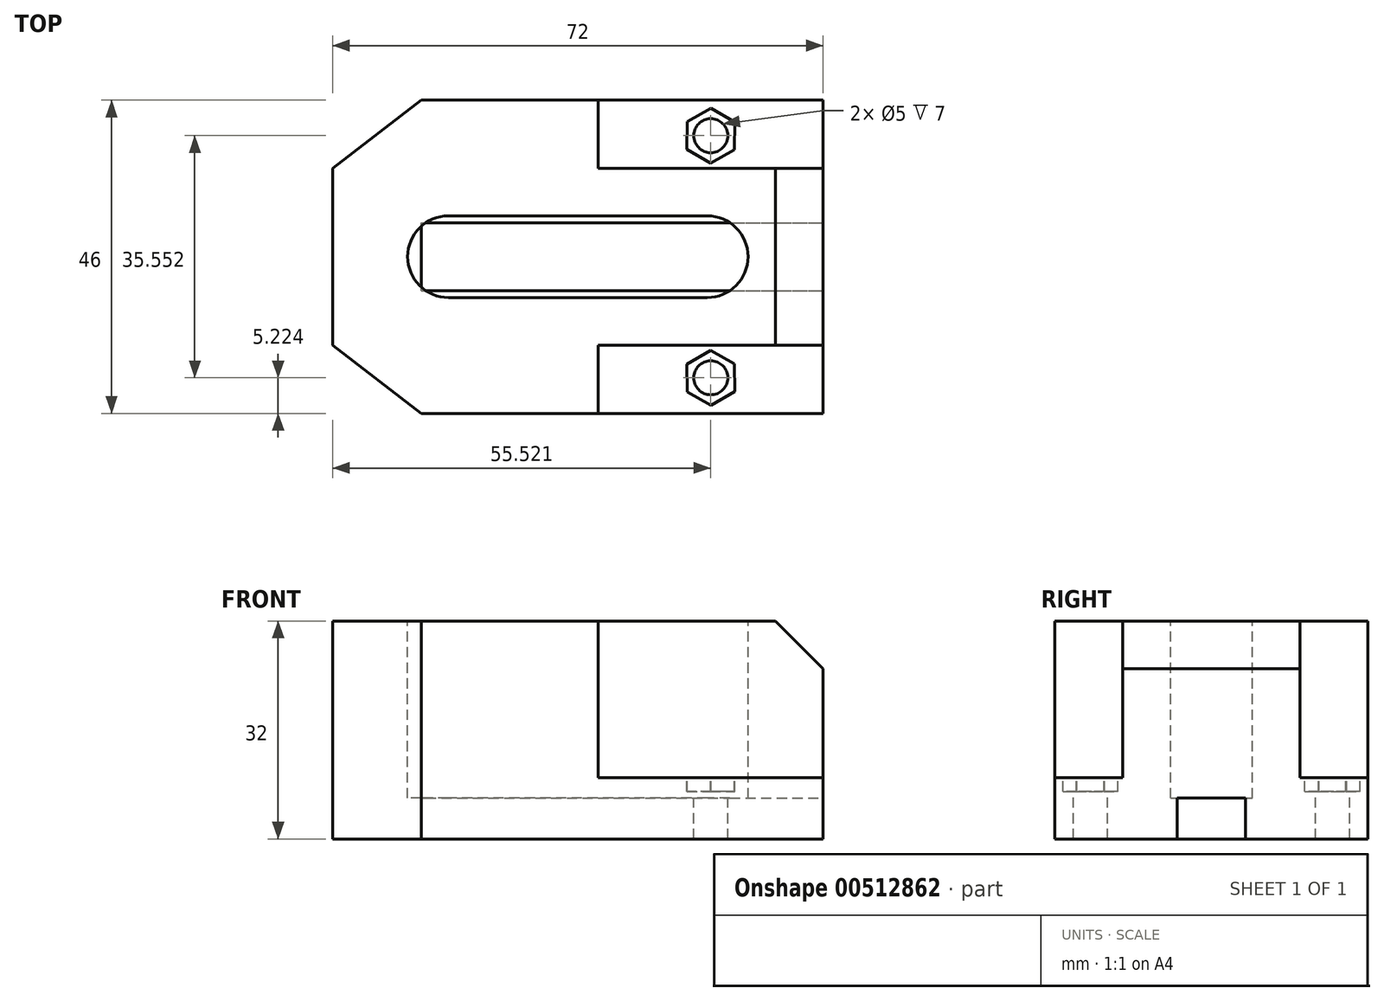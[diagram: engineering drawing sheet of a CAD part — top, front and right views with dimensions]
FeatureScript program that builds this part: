
annotation { "Feature Type Name" : "Feature", "Feature Type Description" : "" }
export const myFeature = defineFeature(function(context is Context, id is Id, definition is map)
    precondition{}
    {
        {
            var Q0;
            Q0=qCreatedBy(makeId("Top.planeOp"),FACE);
            var sketch = newSketch(context, id + "F0", { "sketchPlane" : qUnion([Q0])});
            skLineSegment(sketch, "E0.bottom", {"start": v(29.5, -23) * mm, "end": v(-29.5, -23) * mm});
            skLineSegment(sketch, "E0.top", {"start": v(29.5, 23) * mm, "end": v(-29.5, 23) * mm});
            skLineSegment(sketch, "E0.left", {"start": v(29.5, -23) * mm, "end": v(29.5, 23) * mm});
            skLineSegment(sketch, "E0.right", {"start": v(-29.5, -23) * mm, "end": v(-29.5, 23) * mm});
            skPoint(sketch, "E0.middle", {"position": v(0, 0) * mm});
            skSolve(sketch);
        }
        {
            var Q0;
            Q0 = qSketchRegion(id + "F0", true);
            extrude(context, id + "F1", {"entities" : qUnion([Q0]), "depth" : 32 * mm});
        }
        {
            var Q0;
            Q0=makeQuery(id+"F1.opExtrude","SWEPT_FACE",FACE,{"disambiguationData":[OSD([sQuery(id+"F0.wireOp",EDGE,"E0.left")])]});
            var sketch = newSketch(context, id + "F2", { "sketchPlane" : qUnion([Q0])});
            skLineSegment(sketch, "E1.bottom", {"start": v(-5, 0) * mm, "end": v(5, 0) * mm});
            skLineSegment(sketch, "E1.top", {"start": v(-5, 6) * mm, "end": v(5, 6) * mm});
            skLineSegment(sketch, "E1.left", {"start": v(-5, 0) * mm, "end": v(-5, 6) * mm});
            skLineSegment(sketch, "E1.right", {"start": v(5, 0) * mm, "end": v(5, 6) * mm});
            skSolve(sketch);
        }
        {
            var Q0;
            Q0 = qSketchRegion(id + "F2", true);
            extrude(context, id + "F3", {"entities" : qUnion([Q0]), "operationType" : NewBodyOperationType.REMOVE, "oppositeDirection" : true, "depth" : 59 * mm});
        }
        {
            var Q0;
            Q0=makeQuery(id+"F1.opExtrude","CAP_FACE",FACE,{"disambiguationData":[OSD([sQuery(id+"F0.wireOp",EDGE,"E0.bottom"),sQuery(id+"F0.wireOp",EDGE,"E0.top"),sQuery(id+"F0.wireOp",EDGE,"E0.left"),sQuery(id+"F0.wireOp",EDGE,"E0.right")])],"isStart":false});
            var sketch = newSketch(context, id + "F4", { "sketchPlane" : qUnion([Q0])});
            skLineSegment(sketch, "E2.bottom", {"start": v(29.5, -23) * mm, "end": v(-3.5, -23) * mm});
            skLineSegment(sketch, "E2.top", {"start": v(29.5, -13) * mm, "end": v(-3.5, -13) * mm});
            skLineSegment(sketch, "E2.left", {"start": v(29.5, -23) * mm, "end": v(29.5, -13) * mm});
            skLineSegment(sketch, "E2.right", {"start": v(-3.5, -23) * mm, "end": v(-3.5, -13) * mm});
            skLineSegment(sketch, "E3", {"start": v(0, 0) * mm, "end": v(-20.52, 0) * mm, "construction": true});
            skLineSegment(sketch, "E4.MirrorCS", {"start": v(29.5, 13) * mm, "end": v(-3.5, 13) * mm});
            skLineSegment(sketch, "E5.MirrorCS", {"start": v(-3.5, 23) * mm, "end": v(-3.5, 13) * mm});
            skLineSegment(sketch, "E6.MirrorCS", {"start": v(29.5, 23) * mm, "end": v(-3.5, 23) * mm});
            skLineSegment(sketch, "E7.MirrorCS", {"start": v(29.5, 23) * mm, "end": v(29.5, 13) * mm});
            skLineSegment(sketch, "E8", {"start": v(-42.5, -13) * mm, "end": v(-42.5, 13) * mm});
            skLineSegment(sketch, "E9", {"start": v(-42.5, -13) * mm, "end": v(-29.5, -23) * mm});
            skLineSegment(sketch, "E10", {"start": v(-42.5, 13) * mm, "end": v(-29.5, 23) * mm});
            skSolve(sketch);
        }
        {
            var Q0;
            Q0 = qSketchRegion(id + "F4", true);
            extrude(context, id + "F5", {"entities" : qUnion([Q0]), "operationType" : NewBodyOperationType.REMOVE, "oppositeDirection" : true, "depth" : 23 * mm});
        }
        {
            var Q0;
            Q0=makeQuery(id+"F4.imprint","IMPRINT",FACE,{"disambiguationData":[TD([[makeQuery(id+"F4.imprint","IMPRINT",EDGE,{"derivedFrom":sQuery(id+"F4.wireOp",EDGE,"E8")}),-1.0]])]});
            extrude(context, id + "F6", {"entities" : qUnion([Q0]), "operationType" : NewBodyOperationType.ADD, "oppositeDirection" : true, "depth" : 32 * mm});
        }
        {
            var Q0;
            Q0=makeQuery(id+"F5.boolean.opBoolean","COPY",FACE,{"derivedFrom":makeQuery(id+"F5.opExtrude","SWEPT_FACE",FACE,{"disambiguationData":[OSD([sQuery(id+"F4.wireOp",EDGE,"E2.top")])]})});
            var sketch = newSketch(context, id + "F7", { "sketchPlane" : qUnion([Q0])});
            skLineSegment(sketch, "E11", {"start": v(29.5, 32) * mm, "end": v(29.5, 25) * mm});
            skLineSegment(sketch, "E12", {"start": v(29.5, 25) * mm, "end": v(22.5, 32) * mm});
            skLineSegment(sketch, "E13", {"start": v(22.5, 32) * mm, "end": v(29.5, 32) * mm});
            skSolve(sketch);
        }
        {
            var Q0;
            Q0 = qSketchRegion(id + "F7", true);
            extrude(context, id + "F8", {"entities" : qUnion([Q0]), "operationType" : NewBodyOperationType.REMOVE, "oppositeDirection" : true, "depth" : 26 * mm});
        }
        {
            var Q0;
            {var subQ4=sQuery(id+"F4.wireOp",EDGE,"E2.top");Q0=makeQuery(id+"F4.imprint","IMPRINT",FACE,{"disambiguationData":[TD([[makeQuery(id+"F4.imprint","IMPRINT",EDGE,{"derivedFrom":subQ4}),-1.0]])]});}
            var sketch = newSketch(context, id + "F9", { "sketchPlane" : qUnion([Q0])});
            skLineSegment(sketch, "E14", {"start": v(-3.5, 13) * mm, "end": v(-3.5, -13) * mm});
            skLineSegment(sketch, "E15.bottom", {"start": v(12.5, -6) * mm, "end": v(-25.5, -6) * mm});
            skLineSegment(sketch, "E15.top", {"start": v(12.5, 6) * mm, "end": v(-25.5, 6) * mm});
            skLineSegment(sketch, "E15.left", {"start": v(12.5, -6) * mm, "end": v(12.5, 6) * mm});
            skLineSegment(sketch, "E15.right", {"start": v(-25.5, -6) * mm, "end": v(-25.5, 6) * mm});
            skArc(sketch, "E16", {"start": v(12.5, -6) * mm, "mid": v(18.5, 0) * mm, "end": v(12.5, 6) * mm});
            skArc(sketch, "E17", {"start": v(-25.5, 6) * mm, "mid": v(-31.5, 0) * mm, "end": v(-25.5, -6) * mm});
            skSolve(sketch);
        }
        {
            var Q0;
            Q0 = qSketchRegion(id + "F9", true);
            extrude(context, id + "F10", {"entities" : qUnion([Q0]), "operationType" : NewBodyOperationType.REMOVE, "oppositeDirection" : true, "depth" : 26 * mm});
        }
        {
            var Q0;
            Q0=makeQuery(id+"F5.boolean.opBoolean","COPY",FACE,{"derivedFrom":makeQuery(id+"F5.opExtrude","CAP_FACE",FACE,{"disambiguationData":[OSD([sQuery(id+"F4.wireOp",EDGE,"E2.bottom"),sQuery(id+"F4.wireOp",EDGE,"E2.top"),sQuery(id+"F4.wireOp",EDGE,"E2.left"),sQuery(id+"F4.wireOp",EDGE,"E2.right")])],"isStart":false})});
            var sketch = newSketch(context, id + "F11", { "sketchPlane" : qUnion([Q0])});
            skCircle(sketch, "E18.cCircle", {"center": v(13.02, -17.78) * mm, "radius": 3.5 * mm, "construction": true});
            skLineSegment(sketch, "E18.0", {"start": v(12.98, -13.73) * mm, "end": v(16.5, -15.72) * mm});
            skLineSegment(sketch, "E18.1", {"start": v(16.5, -15.72) * mm, "end": v(16.54, -19.76) * mm});
            skLineSegment(sketch, "E18.2", {"start": v(16.54, -19.76) * mm, "end": v(13.06, -21.82) * mm});
            skLineSegment(sketch, "E18.3", {"start": v(13.06, -21.82) * mm, "end": v(9.54, -19.83) * mm});
            skLineSegment(sketch, "E18.4", {"start": v(9.54, -19.83) * mm, "end": v(9.5, -15.8) * mm});
            skLineSegment(sketch, "E18.5", {"start": v(9.5, -15.8) * mm, "end": v(12.98, -13.73) * mm});
            skPoint(sketch, "E18.0.midPoint", {"position": v(14.74, -14.73) * mm});
            skCircle(sketch, "E19.MirrorC", {"center": v(13.02, 17.78) * mm, "radius": 3.5 * mm, "construction": true});
            skLineSegment(sketch, "E20.MirrorCS", {"start": v(9.54, 19.83) * mm, "end": v(9.5, 15.8) * mm});
            skLineSegment(sketch, "E21.MirrorCS", {"start": v(9.5, 15.8) * mm, "end": v(12.98, 13.73) * mm});
            skLineSegment(sketch, "E22.MirrorCS", {"start": v(12.98, 13.73) * mm, "end": v(16.5, 15.72) * mm});
            skLineSegment(sketch, "E23.MirrorCS", {"start": v(16.5, 15.72) * mm, "end": v(16.54, 19.76) * mm});
            skLineSegment(sketch, "E24.MirrorCS", {"start": v(16.54, 19.76) * mm, "end": v(13.06, 21.82) * mm});
            skLineSegment(sketch, "E25.MirrorCS", {"start": v(13.06, 21.82) * mm, "end": v(9.54, 19.83) * mm});
            skSolve(sketch);
        }
        {
            var Q0;
            Q0 = qSketchRegion(id + "F11", true);
            extrude(context, id + "F12", {"entities" : qUnion([Q0]), "operationType" : NewBodyOperationType.REMOVE, "oppositeDirection" : true, "depth" : 2 * mm});
        }
        {
            var Q0;
            Q0=makeQuery(id+"F12.boolean.opBoolean","COPY",FACE,{"derivedFrom":makeQuery(id+"F12.opExtrude","CAP_FACE",FACE,{"disambiguationData":[OSD([sQuery(id+"F11.wireOp",EDGE,"E18.0"),sQuery(id+"F11.wireOp",EDGE,"E18.1"),sQuery(id+"F11.wireOp",EDGE,"E18.2"),sQuery(id+"F11.wireOp",EDGE,"E18.3"),sQuery(id+"F11.wireOp",EDGE,"E18.4"),sQuery(id+"F11.wireOp",EDGE,"E18.5")])],"isStart":false})});
            var sketch = newSketch(context, id + "F13", { "sketchPlane" : qUnion([Q0])});
            skLineSegment(sketch, "E26", {"start": v(12.98, -13.73) * mm, "end": v(13.06, -21.82) * mm});
            skCircle(sketch, "E27", {"center": v(13.02, -17.78) * mm, "radius": 2.5 * mm});
            skCircle(sketch, "E28.MirrorC", {"center": v(13.02, 17.78) * mm, "radius": 2.5 * mm});
            skSolve(sketch);
        }
        {
            var Q0;
            Q0 = qSketchRegion(id + "F13", true);
            extrude(context, id + "F14", {"entities" : qUnion([Q0]), "operationType" : NewBodyOperationType.REMOVE, "oppositeDirection" : true, "depth" : 25 * mm});
        }
    });
